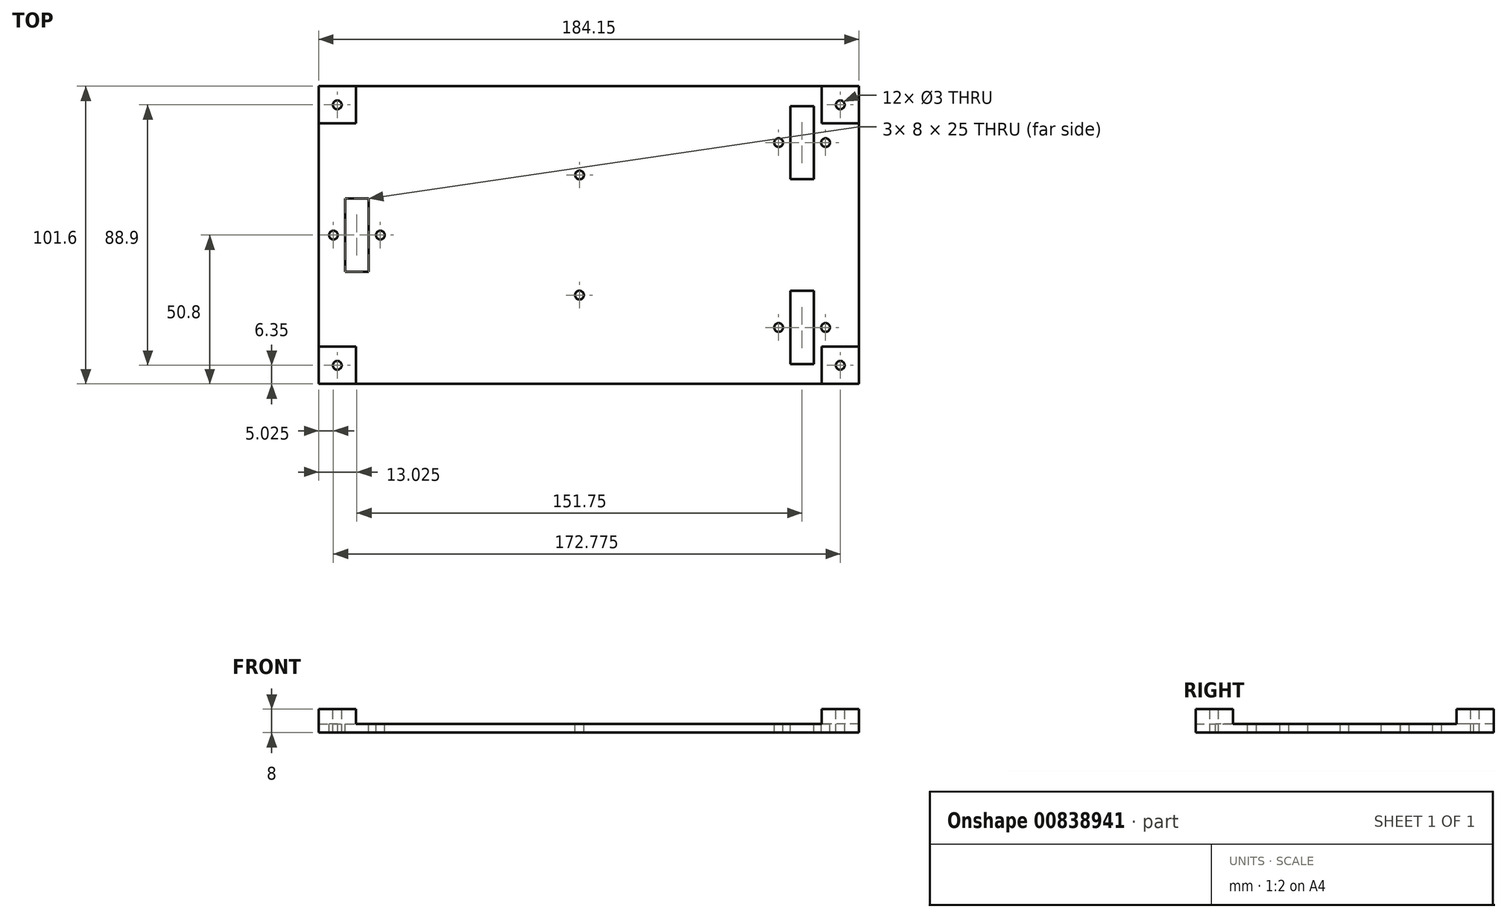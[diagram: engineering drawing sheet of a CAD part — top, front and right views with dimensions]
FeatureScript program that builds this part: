
annotation { "Feature Type Name" : "Feature", "Feature Type Description" : "" }
export const myFeature = defineFeature(function(context is Context, id is Id, definition is map)
    precondition{}
    {
        {
            var Q0;
            Q0=qCreatedBy(makeId("Top.planeOp"),FACE);
            var sketch = newSketch(context, id + "F0", { "sketchPlane" : qUnion([Q0])});
            skLineSegment(sketch, "E0.bottom", {"start": v(-88.9, 50.8) * mm, "end": v(95.25, 50.8) * mm});
            skLineSegment(sketch, "E0.top", {"start": v(-88.9, -50.8) * mm, "end": v(95.25, -50.8) * mm});
            skLineSegment(sketch, "E0.left", {"start": v(-88.9, 50.8) * mm, "end": v(-88.9, -50.8) * mm});
            skLineSegment(sketch, "E0.right", {"start": v(95.25, 50.8) * mm, "end": v(95.25, -50.8) * mm});
            skSolve(sketch);
        }
        {
            var Q0;
            Q0 = qSketchRegion(id + "F0", true);
            extrude(context, id + "F1", {"entities" : qUnion([Q0]), "depth" : 3 * mm, "offsetDistance" : 25.4 * mm});
        }
        {
            var Q0;
            Q0=qCreatedBy(makeId("Top.planeOp"),FACE);
            var sketch = newSketch(context, id + "F2", { "sketchPlane" : qUnion([Q0])});
            skPoint(sketch, "E1.middle", {"position": v(-1.08, 0.31) * mm});
            skCircle(sketch, "E2", {"center": v(-105.58, 104.81) * mm, "radius": 1.5 * mm});
            skCircle(sketch, "E3", {"center": v(103.42, 104.81) * mm, "radius": 1.5 * mm});
            skCircle(sketch, "E4", {"center": v(103.42, -104.19) * mm, "radius": 1.5 * mm});
            skCircle(sketch, "E5", {"center": v(-105.58, -104.19) * mm, "radius": 1.5 * mm});
            skCircle(sketch, "E6", {"center": v(-1.08, 20.81) * mm, "radius": 1.5 * mm});
            skCircle(sketch, "E7", {"center": v(-1.08, -20.19) * mm, "radius": 1.5 * mm});
            skLineSegment(sketch, "E8.bottom", {"start": v(88.52, 15.31) * mm, "end": v(84.32, 15.31) * mm});
            skLineSegment(sketch, "E8.top", {"start": v(88.52, -14.69) * mm, "end": v(84.32, -14.69) * mm});
            skLineSegment(sketch, "E8.left", {"start": v(91.52, 12.31) * mm, "end": v(91.52, -11.69) * mm});
            skLineSegment(sketch, "E8.right", {"start": v(81.32, 12.31) * mm, "end": v(81.32, -11.69) * mm});
            skPoint(sketch, "E8.middle", {"position": v(86.42, 0.31) * mm});
            skLineSegment(sketch, "E9.bottom", {"start": v(-86.48, 25.31) * mm, "end": v(-90.68, 25.31) * mm});
            skLineSegment(sketch, "E9.top", {"start": v(-86.48, 55.31) * mm, "end": v(-90.68, 55.31) * mm});
            skLineSegment(sketch, "E9.left", {"start": v(-83.48, 28.31) * mm, "end": v(-83.48, 52.31) * mm});
            skLineSegment(sketch, "E9.right", {"start": v(-93.68, 28.31) * mm, "end": v(-93.68, 52.31) * mm});
            skPoint(sketch, "E9.middle", {"position": v(-88.58, 40.31) * mm});
            skLineSegment(sketch, "E10.bottom", {"start": v(-86.48, -24.69) * mm, "end": v(-90.68, -24.69) * mm});
            skLineSegment(sketch, "E10.top", {"start": v(-86.48, -54.69) * mm, "end": v(-90.68, -54.69) * mm});
            skLineSegment(sketch, "E10.left", {"start": v(-83.48, -27.69) * mm, "end": v(-83.48, -51.69) * mm});
            skLineSegment(sketch, "E10.right", {"start": v(-93.68, -27.69) * mm, "end": v(-93.68, -51.69) * mm});
            skPoint(sketch, "E10.middle", {"position": v(-88.58, -39.69) * mm});
            skPoint(sketch, "E11.visualSharp", {"position": v(-93.68, 55.31) * mm});
            skArc(sketch, "E11.filletArc", {"start": v(-90.68, 55.31) * mm, "mid": v(-92.8, 54.43) * mm, "end": v(-93.68, 52.31) * mm});
            skPoint(sketch, "E12.visualSharp", {"position": v(-83.48, 55.31) * mm});
            skArc(sketch, "E12.filletArc", {"start": v(-83.48, 52.31) * mm, "mid": v(-84.36, 54.43) * mm, "end": v(-86.48, 55.31) * mm});
            skPoint(sketch, "E13.visualSharp", {"position": v(-83.48, 25.31) * mm});
            skArc(sketch, "E13.filletArc", {"start": v(-86.48, 25.31) * mm, "mid": v(-84.36, 26.19) * mm, "end": v(-83.48, 28.31) * mm});
            skPoint(sketch, "E14.visualSharp", {"position": v(-93.68, 25.31) * mm});
            skArc(sketch, "E14.filletArc", {"start": v(-93.68, 28.31) * mm, "mid": v(-92.8, 26.19) * mm, "end": v(-90.68, 25.31) * mm});
            skPoint(sketch, "E15.visualSharp", {"position": v(-83.48, -24.69) * mm});
            skArc(sketch, "E15.filletArc", {"start": v(-83.48, -27.69) * mm, "mid": v(-84.36, -25.57) * mm, "end": v(-86.48, -24.69) * mm});
            skPoint(sketch, "E16.visualSharp", {"position": v(-93.68, -24.69) * mm});
            skArc(sketch, "E16.filletArc", {"start": v(-90.68, -24.69) * mm, "mid": v(-92.8, -25.57) * mm, "end": v(-93.68, -27.69) * mm});
            skPoint(sketch, "E17.visualSharp", {"position": v(-93.68, -54.69) * mm});
            skArc(sketch, "E17.filletArc", {"start": v(-93.68, -51.69) * mm, "mid": v(-92.8, -53.81) * mm, "end": v(-90.68, -54.69) * mm});
            skPoint(sketch, "E18.visualSharp", {"position": v(-83.48, -54.69) * mm});
            skArc(sketch, "E18.filletArc", {"start": v(-86.48, -54.69) * mm, "mid": v(-84.36, -53.81) * mm, "end": v(-83.48, -51.69) * mm});
            skPoint(sketch, "E19.visualSharp", {"position": v(91.52, -14.69) * mm});
            skArc(sketch, "E19.filletArc", {"start": v(88.52, -14.69) * mm, "mid": v(90.64, -13.81) * mm, "end": v(91.52, -11.69) * mm});
            skPoint(sketch, "E20.visualSharp", {"position": v(81.32, -14.69) * mm});
            skArc(sketch, "E20.filletArc", {"start": v(81.32, -11.69) * mm, "mid": v(82.2, -13.81) * mm, "end": v(84.32, -14.69) * mm});
            skPoint(sketch, "E21.visualSharp", {"position": v(81.32, 15.31) * mm});
            skArc(sketch, "E21.filletArc", {"start": v(84.32, 15.31) * mm, "mid": v(82.2, 14.43) * mm, "end": v(81.32, 12.31) * mm});
            skPoint(sketch, "E22.visualSharp", {"position": v(91.52, 15.31) * mm});
            skArc(sketch, "E22.filletArc", {"start": v(91.52, 12.31) * mm, "mid": v(90.64, 14.43) * mm, "end": v(88.52, 15.31) * mm});
            skCircle(sketch, "E23", {"center": v(-78.58, 40.31) * mm, "radius": 2.25 * mm});
            skCircle(sketch, "E24", {"center": v(-98.58, 40.31) * mm, "radius": 2.25 * mm});
            skCircle(sketch, "E25", {"center": v(-78.58, -39.69) * mm, "radius": 2.25 * mm});
            skCircle(sketch, "E26", {"center": v(-98.58, -39.69) * mm, "radius": 2.25 * mm});
            skCircle(sketch, "E27", {"center": v(96.42, 0.31) * mm, "radius": 2.25 * mm});
            skCircle(sketch, "E28", {"center": v(76.42, 0.31) * mm, "radius": 2.25 * mm});
            skLineSegment(sketch, "E29.bottom", {"start": v(-105.58, 112.31) * mm, "end": v(103.42, 112.31) * mm});
            skLineSegment(sketch, "E29.top", {"start": v(-105.58, -111.69) * mm, "end": v(103.42, -111.69) * mm});
            skLineSegment(sketch, "E29.left", {"start": v(-113.08, 104.81) * mm, "end": v(-113.08, -104.19) * mm});
            skLineSegment(sketch, "E29.right", {"start": v(110.92, 104.81) * mm, "end": v(110.92, -104.19) * mm});
            skPoint(sketch, "E30.visualSharp", {"position": v(-113.08, 112.31) * mm});
            skArc(sketch, "E30.filletArc", {"start": v(-105.58, 112.31) * mm, "mid": v(-110.88, 110.11) * mm, "end": v(-113.08, 104.81) * mm});
            skPoint(sketch, "E31.visualSharp", {"position": v(110.92, 112.31) * mm});
            skArc(sketch, "E31.filletArc", {"start": v(110.92, 104.81) * mm, "mid": v(108.73, 110.11) * mm, "end": v(103.42, 112.31) * mm});
            skPoint(sketch, "E32.visualSharp", {"position": v(110.92, -111.69) * mm});
            skArc(sketch, "E32.filletArc", {"start": v(103.42, -111.69) * mm, "mid": v(108.73, -109.5) * mm, "end": v(110.92, -104.19) * mm});
            skPoint(sketch, "E33.visualSharp", {"position": v(-113.08, -111.69) * mm});
            skArc(sketch, "E33.filletArc", {"start": v(-113.08, -104.19) * mm, "mid": v(-110.88, -109.5) * mm, "end": v(-105.58, -111.69) * mm});
            skLineSegment(sketch, "E34", {"start": v(-113.08, 112.31) * mm, "end": v(110.92, -111.69) * mm, "construction": true});
            skLineSegment(sketch, "E35", {"start": v(110.92, 112.31) * mm, "end": v(-113.08, -111.69) * mm, "construction": true});
            skLineSegment(sketch, "E36.left", {"start": v(3.92, 91.31) * mm, "end": v(3.92, 46.31) * mm});
            skLineSegment(sketch, "E36.right", {"start": v(-6.08, 91.31) * mm, "end": v(-6.08, 46.31) * mm});
            skLineSegment(sketch, "E37", {"start": v(-69.45, 97.31) * mm, "end": v(-12.08, 97.31) * mm});
            skLineSegment(sketch, "E38", {"start": v(9.92, 97.31) * mm, "end": v(67.3, 97.31) * mm});
            skLineSegment(sketch, "E39", {"start": v(-12.08, 40.31) * mm, "end": v(-24.45, 40.31) * mm});
            skLineSegment(sketch, "E40", {"start": v(9.92, 40.31) * mm, "end": v(22.3, 40.31) * mm});
            skPoint(sketch, "E41.visualSharp", {"position": v(-6.08, 97.31) * mm});
            skArc(sketch, "E41.filletArc", {"start": v(-6.08, 91.31) * mm, "mid": v(-7.83, 95.55) * mm, "end": v(-12.08, 97.31) * mm});
            skPoint(sketch, "E42.visualSharp", {"position": v(-6.08, 40.31) * mm});
            skArc(sketch, "E42.filletArc", {"start": v(-12.08, 40.31) * mm, "mid": v(-7.83, 42.07) * mm, "end": v(-6.08, 46.31) * mm});
            skLineSegment(sketch, "E43", {"start": v(-73.7, 87.07) * mm, "end": v(-28.7, 42.07) * mm});
            skPoint(sketch, "E44.visualSharp", {"position": v(-26.93, 40.31) * mm});
            skArc(sketch, "E44.filletArc", {"start": v(-28.7, 42.07) * mm, "mid": v(-26.75, 40.77) * mm, "end": v(-24.45, 40.31) * mm});
            skPoint(sketch, "E45.visualSharp", {"position": v(-83.93, 97.31) * mm});
            skArc(sketch, "E45.filletArc", {"start": v(-69.45, 97.31) * mm, "mid": v(-75, 93.6) * mm, "end": v(-73.7, 87.07) * mm});
            skLineSegment(sketch, "E46", {"start": v(71.54, 87.07) * mm, "end": v(26.54, 42.07) * mm});
            skPoint(sketch, "E47.visualSharp", {"position": v(3.92, 97.31) * mm});
            skArc(sketch, "E47.filletArc", {"start": v(9.92, 97.31) * mm, "mid": v(5.68, 95.55) * mm, "end": v(3.92, 91.31) * mm});
            skPoint(sketch, "E48.visualSharp", {"position": v(81.78, 97.31) * mm});
            skArc(sketch, "E48.filletArc", {"start": v(71.54, 87.07) * mm, "mid": v(72.84, 93.6) * mm, "end": v(67.3, 97.31) * mm});
            skPoint(sketch, "E49.visualSharp", {"position": v(24.78, 40.31) * mm});
            skArc(sketch, "E49.filletArc", {"start": v(22.3, 40.31) * mm, "mid": v(24.6, 40.77) * mm, "end": v(26.54, 42.07) * mm});
            skPoint(sketch, "E50.visualSharp", {"position": v(3.92, 40.31) * mm});
            skArc(sketch, "E50.filletArc", {"start": v(3.92, 46.31) * mm, "mid": v(5.68, 42.07) * mm, "end": v(9.92, 40.31) * mm});
            skLineSegment(sketch, "E51", {"start": v(49.17, 36.41) * mm, "end": v(85.68, 72.93) * mm});
            skLineSegment(sketch, "E52", {"start": v(95.92, 68.68) * mm, "end": v(95.92, 32.17) * mm});
            skPoint(sketch, "E53.visualSharp", {"position": v(95.92, 83.17) * mm});
            skArc(sketch, "E53.filletArc", {"start": v(95.92, 68.68) * mm, "mid": v(92.22, 74.23) * mm, "end": v(85.68, 72.93) * mm});
            skPoint(sketch, "E54.visualSharp", {"position": v(38.92, 26.17) * mm});
            skLineSegment(sketch, "E55", {"start": v(85.68, -72.3) * mm, "end": v(49.17, -35.79) * mm});
            skLineSegment(sketch, "E56", {"start": v(53.4, -25.55) * mm, "end": v(89.92, -25.55) * mm});
            skLineSegment(sketch, "E57", {"start": v(95.92, -31.55) * mm, "end": v(95.92, -68.06) * mm});
            skLineSegment(sketch, "E58", {"start": v(53.4, 26.17) * mm, "end": v(89.92, 26.17) * mm});
            skPoint(sketch, "E59.visualSharp", {"position": v(95.92, 26.17) * mm});
            skArc(sketch, "E59.filletArc", {"start": v(89.92, 26.17) * mm, "mid": v(94.17, 27.93) * mm, "end": v(95.92, 32.17) * mm});
            skArc(sketch, "E60.filletArc", {"start": v(49.17, 36.41) * mm, "mid": v(47.87, 29.87) * mm, "end": v(53.4, 26.17) * mm});
            skPoint(sketch, "E61.visualSharp", {"position": v(95.92, -25.55) * mm});
            skArc(sketch, "E61.filletArc", {"start": v(95.92, -31.55) * mm, "mid": v(94.17, -27.3) * mm, "end": v(89.92, -25.55) * mm});
            skPoint(sketch, "E62.visualSharp", {"position": v(38.92, -25.55) * mm});
            skArc(sketch, "E62.filletArc", {"start": v(53.4, -25.55) * mm, "mid": v(47.87, -29.25) * mm, "end": v(49.17, -35.79) * mm});
            skPoint(sketch, "E63.visualSharp", {"position": v(95.92, -82.55) * mm});
            skArc(sketch, "E63.filletArc", {"start": v(85.68, -72.3) * mm, "mid": v(92.22, -73.6) * mm, "end": v(95.92, -68.06) * mm});
            skLineSegment(sketch, "E64", {"start": v(-113.08, 0.31) * mm, "end": v(110.92, 0.31) * mm, "construction": true});
            skLineSegment(sketch, "E65", {"start": v(26.54, -41.45) * mm, "end": v(71.54, -86.45) * mm});
            skLineSegment(sketch, "E66", {"start": v(-28.7, -41.45) * mm, "end": v(-73.7, -86.45) * mm});
            skLineSegment(sketch, "E67.left", {"start": v(3.92, -45.69) * mm, "end": v(3.92, -90.69) * mm});
            skLineSegment(sketch, "E67.right", {"start": v(-6.08, -45.69) * mm, "end": v(-6.08, -90.69) * mm});
            skPoint(sketch, "E67.middle", {"position": v(-1.08, -68.19) * mm});
            skLineSegment(sketch, "E68", {"start": v(-12.08, -96.69) * mm, "end": v(-69.45, -96.69) * mm});
            skLineSegment(sketch, "E69", {"start": v(-12.08, -39.69) * mm, "end": v(-24.45, -39.69) * mm});
            skLineSegment(sketch, "E70", {"start": v(9.92, -96.69) * mm, "end": v(67.3, -96.69) * mm});
            skLineSegment(sketch, "E71", {"start": v(9.92, -39.69) * mm, "end": v(22.3, -39.69) * mm});
            skPoint(sketch, "E72.visualSharp", {"position": v(-6.08, -39.69) * mm});
            skArc(sketch, "E72.filletArc", {"start": v(-6.08, -45.69) * mm, "mid": v(-7.83, -41.45) * mm, "end": v(-12.08, -39.69) * mm});
            skPoint(sketch, "E73.visualSharp", {"position": v(-6.08, -96.69) * mm});
            skArc(sketch, "E73.filletArc", {"start": v(-12.08, -96.69) * mm, "mid": v(-7.83, -94.93) * mm, "end": v(-6.08, -90.69) * mm});
            skPoint(sketch, "E74.visualSharp", {"position": v(-26.93, -39.69) * mm});
            skArc(sketch, "E74.filletArc", {"start": v(-24.45, -39.69) * mm, "mid": v(-26.75, -40.15) * mm, "end": v(-28.7, -41.45) * mm});
            skPoint(sketch, "E75.visualSharp", {"position": v(3.92, -96.69) * mm});
            skArc(sketch, "E75.filletArc", {"start": v(3.92, -90.69) * mm, "mid": v(5.68, -94.93) * mm, "end": v(9.92, -96.69) * mm});
            skPoint(sketch, "E76.visualSharp", {"position": v(81.78, -96.69) * mm});
            skArc(sketch, "E76.filletArc", {"start": v(67.3, -96.69) * mm, "mid": v(72.84, -92.98) * mm, "end": v(71.54, -86.45) * mm});
            skPoint(sketch, "E77.visualSharp", {"position": v(24.78, -39.69) * mm});
            skArc(sketch, "E77.filletArc", {"start": v(26.54, -41.45) * mm, "mid": v(24.6, -40.15) * mm, "end": v(22.3, -39.69) * mm});
            skPoint(sketch, "E78.visualSharp", {"position": v(-83.93, -96.69) * mm});
            skArc(sketch, "E78.filletArc", {"start": v(-73.7, -86.45) * mm, "mid": v(-75, -92.98) * mm, "end": v(-69.45, -96.69) * mm});
            skPoint(sketch, "E79.visualSharp", {"position": v(3.92, -39.69) * mm});
            skArc(sketch, "E79.filletArc", {"start": v(9.92, -39.69) * mm, "mid": v(5.68, -41.45) * mm, "end": v(3.92, -45.69) * mm});
            skSolve(sketch);
        }
        {
            var Q0;
            Q0=makeQuery(id+"F1.opExtrude","CAP_FACE",FACE,{"disambiguationData":[OSD([sQuery(id+"F0.wireOp",EDGE,"E0.bottom"),sQuery(id+"F0.wireOp",EDGE,"E0.top"),sQuery(id+"F0.wireOp",EDGE,"E0.left"),sQuery(id+"F0.wireOp",EDGE,"E0.right")])],"isStart":false});
            var sketch = newSketch(context, id + "F3", { "sketchPlane" : qUnion([Q0])});
            skLineSegment(sketch, "E80.bottom", {"start": v(71.88, 44.05) * mm, "end": v(79.87, 44.05) * mm});
            skLineSegment(sketch, "E80.top", {"start": v(71.88, 19.05) * mm, "end": v(79.87, 19.05) * mm});
            skLineSegment(sketch, "E80.left", {"start": v(71.88, 44.05) * mm, "end": v(71.88, 19.05) * mm});
            skLineSegment(sketch, "E80.right", {"start": v(79.87, 44.05) * mm, "end": v(79.87, 19.05) * mm});
            skLineSegment(sketch, "E81.bottom", {"start": v(-79.88, 12.5) * mm, "end": v(-71.88, 12.5) * mm});
            skLineSegment(sketch, "E81.top", {"start": v(-79.88, -12.5) * mm, "end": v(-71.88, -12.5) * mm});
            skLineSegment(sketch, "E81.left", {"start": v(-79.88, 12.5) * mm, "end": v(-79.88, -12.5) * mm});
            skLineSegment(sketch, "E81.right", {"start": v(-71.88, 12.5) * mm, "end": v(-71.88, -12.5) * mm});
            skLineSegment(sketch, "E82.bottom", {"start": v(71.88, -19.05) * mm, "end": v(79.88, -19.05) * mm});
            skLineSegment(sketch, "E82.top", {"start": v(71.88, -44.05) * mm, "end": v(79.88, -44.05) * mm});
            skLineSegment(sketch, "E82.left", {"start": v(71.88, -19.05) * mm, "end": v(71.88, -44.05) * mm});
            skLineSegment(sketch, "E82.right", {"start": v(79.88, -19.05) * mm, "end": v(79.88, -44.05) * mm});
            skCircle(sketch, "E83", {"center": v(-67.87, 0) * mm, "radius": 1.5 * mm});
            skCircle(sketch, "E84", {"center": v(-83.88, 0) * mm, "radius": 1.5 * mm});
            skCircle(sketch, "E85", {"center": v(83.87, 31.55) * mm, "radius": 1.5 * mm});
            skCircle(sketch, "E86", {"center": v(67.87, 31.55) * mm, "radius": 1.5 * mm});
            skCircle(sketch, "E87", {"center": v(83.88, -31.55) * mm, "radius": 1.5 * mm});
            skCircle(sketch, "E88", {"center": v(67.87, -31.55) * mm, "radius": 1.5 * mm});
            skCircle(sketch, "E89", {"center": v(0.03, 20.5) * mm, "radius": 1.5 * mm});
            skCircle(sketch, "E90", {"center": v(0, -20.5) * mm, "radius": 1.5 * mm});
            skSolve(sketch);
        }
        {
            var Q0;
            Q0 = qSketchRegion(id + "F3", true);
            var Q1;
            Q1 = qSketchRegion(id + "F2", true);
            extrude(context, id + "F4", {"entities" : qUnion([Q0, Q1]), "operationType" : NewBodyOperationType.REMOVE, "endBound" : BoundingType.THROUGH_ALL, "oppositeDirection" : true, "depth" : 25.4 * mm, "offsetDistance" : 25.4 * mm});
        }
        {
            var Q0;
            Q0=makeQuery(id+"F1.opExtrude","CAP_FACE",FACE,{"disambiguationData":[OSD([sQuery(id+"F0.wireOp",EDGE,"E0.bottom"),sQuery(id+"F0.wireOp",EDGE,"E0.top"),sQuery(id+"F0.wireOp",EDGE,"E0.left"),sQuery(id+"F0.wireOp",EDGE,"E0.right")])],"isStart":false});
            var sketch = newSketch(context, id + "F5", { "sketchPlane" : qUnion([Q0])});
            skLineSegment(sketch, "E91.bottom", {"start": v(95.25, -50.8) * mm, "end": v(82.55, -50.8) * mm});
            skLineSegment(sketch, "E91.top", {"start": v(95.25, -38.1) * mm, "end": v(82.55, -38.1) * mm});
            skLineSegment(sketch, "E91.left", {"start": v(95.25, -50.8) * mm, "end": v(95.25, -38.1) * mm});
            skLineSegment(sketch, "E91.right", {"start": v(82.55, -50.8) * mm, "end": v(82.55, -38.1) * mm});
            skLineSegment(sketch, "E92.bottom", {"start": v(-88.9, -50.8) * mm, "end": v(-76.2, -50.8) * mm});
            skLineSegment(sketch, "E92.top", {"start": v(-88.9, -38.1) * mm, "end": v(-76.2, -38.1) * mm});
            skLineSegment(sketch, "E92.left", {"start": v(-88.9, -50.8) * mm, "end": v(-88.9, -38.1) * mm});
            skLineSegment(sketch, "E92.right", {"start": v(-76.2, -50.8) * mm, "end": v(-76.2, -38.1) * mm});
            skLineSegment(sketch, "E93.bottom", {"start": v(-88.9, 50.8) * mm, "end": v(-76.2, 50.8) * mm});
            skLineSegment(sketch, "E93.top", {"start": v(-88.9, 38.1) * mm, "end": v(-76.2, 38.1) * mm});
            skLineSegment(sketch, "E93.left", {"start": v(-88.9, 50.8) * mm, "end": v(-88.9, 38.1) * mm});
            skLineSegment(sketch, "E93.right", {"start": v(-76.2, 50.8) * mm, "end": v(-76.2, 38.1) * mm});
            skLineSegment(sketch, "E94.bottom", {"start": v(95.25, 50.8) * mm, "end": v(82.55, 50.8) * mm});
            skLineSegment(sketch, "E94.top", {"start": v(95.25, 38.1) * mm, "end": v(82.55, 38.1) * mm});
            skLineSegment(sketch, "E94.left", {"start": v(95.25, 50.8) * mm, "end": v(95.25, 38.1) * mm});
            skLineSegment(sketch, "E94.right", {"start": v(82.55, 50.8) * mm, "end": v(82.55, 38.1) * mm});
            skSolve(sketch);
        }
        {
            var Q0;
            Q0 = qSketchRegion(id + "F5", true);
            extrude(context, id + "F6", {"entities" : qUnion([Q0]), "operationType" : NewBodyOperationType.ADD, "depth" : 5 * mm, "offsetDistance" : 25.4 * mm});
        }
        {
            var Q0;
            Q0=makeQuery(id+"F6.opExtrude","CAP_FACE",FACE,{"disambiguationData":[OSD([sQuery(id+"F5.wireOp",EDGE,"E93.bottom"),sQuery(id+"F5.wireOp",EDGE,"E93.top"),sQuery(id+"F5.wireOp",EDGE,"E93.left"),sQuery(id+"F5.wireOp",EDGE,"E93.right")])],"isStart":false});
            var sketch = newSketch(context, id + "F7", { "sketchPlane" : qUnion([Q0])});
            skCircle(sketch, "E95", {"center": v(-82.55, 44.45) * mm, "radius": 1.5 * mm});
            skCircle(sketch, "E96", {"center": v(88.9, 44.45) * mm, "radius": 1.5 * mm});
            skCircle(sketch, "E97", {"center": v(88.9, -44.45) * mm, "radius": 1.5 * mm});
            skCircle(sketch, "E98", {"center": v(-82.55, -44.45) * mm, "radius": 1.5 * mm});
            skSolve(sketch);
        }
        {
            var Q0;
            Q0 = qSketchRegion(id + "F7", true);
            extrude(context, id + "F8", {"entities" : qUnion([Q0]), "operationType" : NewBodyOperationType.REMOVE, "endBound" : BoundingType.THROUGH_ALL, "oppositeDirection" : true, "depth" : 25.4 * mm, "offsetDistance" : 25.4 * mm});
        }
    });
